# Revit family: Legrand_ElectricFireStopping_EZPathFirestopModule_Series44_Wall
name_source: partatom
category: Equipement spécialisé
units: mm (PartAtom-declared; Revit-internal decimal feet)

## family parameters
Cote de connecteur circulaire = Utiliser le diamètre
Couper avec des vides une fois chargée = Non
Hôte = Mur
Numéro OmniClass = 23.20.50.14
Partagée = Non
Point de calcul de pièce = Non
Titre OmniClass = Firestopping
Toujours verticalement = Oui
Type d'élément = Normal

## types (13) — shared parameters
AirLeakage(UL1479) = 1.57 m3/h 0% cable, 3.24 m3/h 100% cable
AssetType = Fixed
Classification(EN13501-2) = EI 120
ClassificationName = Uniclass2015
ClassificationValue = Ss_25_60_30
Code d'assemblage = D4030900
CodePerformance = Conforms to the European standard EN1366-3, BS476/20, ASTM E814 and DIN4102-9
Color = Red
Description = EZ-Path is a mechanical device that provides fully compliant fire stopping for power and data cable management pathways.
DocumentationInstallationGuide = https://www.legrand.co.uk
DocumentationLiterature = https://specifi.bimstore.co.uk
DocumentationTechnical = https://www.legrand.co.uk
DurationUnit = Years
EZ-Path 1 = Oui
EZPathDevice = Firestop-STI-EZ_Path-Series_44+_Fire_Rated_Pathway
EZPathDeviceHeight = 117 mm
EZPathDeviceWidth = 102 mm
EZPathLoadingHeight = 86 mm
EZPathLoadingWidth = 95 mm
ExpansionBegins = 177 deg C
Fabricant = Legrand Electric Ltd
Features = The modules, which are suitable for all types of wall, can be assembled and installed horizontally or vertically to form a sturdy unit
Finish = Powder Coated
FireRating = Up to 4 Hr
FireResistance(EN1366-3) = 2 Hours
General Conditions of Use = https://export.legrand.com
IfcExportAs = IfcBuildingElementPart
IfcExportType = IfcBuildingElementPartTypeEnum.FIRESTOP
InServiceTemperature = Not to exceed 49 deg C
ManufacturerName = Legrand Electric Ltd
Material = 1.5mm thk Galv Steel
ModelNumber = CM250058
ModelNumberDevice = CM250058
ModelNumberExtensions = CM250178
ModelReference = EZ-Path® Permanent Automatic Mechanical Firestop System (Series 44) Wall
Modèle = EZ-Path® Permanent Automatic Mechanical Firestop System (Series 44) Wall
NBSDescription = Fire stopping systems
NBSObjectName = Legrand Electric Ltd - Fire stopping systems
NBSReference = 30-85-30
NominalHeight = 120 mm
Note d'identification = P12
PlateCutoutCenterWidth = 52 mm
PlateCutoutHeight = 117 mm
PlateEdgeCenterWidth = 89 mm
ProductPage = https://www.legrand.co.uk
ProductionYear = 2017
ReactionToFire(EN13501-1) = Class E
ReferencedStandard = CE Marking, EN 1366-3, ETA 130993
Region = Europe
RetainingPlate = Firestop-STI-EZ_Path-Retaining_Plate
SafetyDataSheet = https://files.stifirestop.com
SecondaryModelNumberDevice = EZD44T
SecondaryModelNumberExtensions = EZD44ES
Shape = Rectangle (Series 44)
ShelfLife = No Limit
SoundInsulation(ASTME90) = STC 54
TPlate = Non
TestedSystems = https://www.legrand.co.uk
URL = https://www.legrand.co.uk
VolumeExpansion = 800%
WallOpeningCenterWidth = 54 mm
WallOpeningHeight = 120 mm
WarrantyDescription = Firestop certification guaranteed throughout the entire lifetime of the electrical installation
WarrantyDurationLabor = 0
WarrantyDurationParts = 0
WarrantyDurationUnit = Years
Weight(Kg) = 2.67 kg
_BSBibleVersion = 15
_CurrentRevision = 2
_DistributedBy = www.bimstore.co.uk
zero-valued in all types: Elévation par défaut, ExpectedLife, TPlateNo, _BimSpecGuid

## per-type parameters (varying)
| type | BIMObjectName | Commentaires du type | EZ-Path 2 | EZ-Path 3 | EZ-Path 4 | EZ-Path 5 | EZPathCenterOfGang | ModelNumberBrackets | NoOfDevices | NominalWidth | Plate | PlateCutoutWidth | PlateHeight | PlateNo | PlateWidth | SecondaryModelNumberBrackets | Size | TypeName | WallOpeningWidth |
| 1 Device Cast In Place (Concrete Walls Only) Ref 250058 | Legrand_ElectricFireStopping_EZPathFirestopModule_Series44_Wall_1DeviceCastInPlace | 1 Device Cast In Place (Concrete Walls Only) | Non | Non | Non | Non | 51 mm |  | 1 | 108 mm | Non | 105 mm | 270 mm | 0 | 178 mm |  | 120x108mm | 1 Device Cast In Place (Concrete Walls Only) | 108 mm |
| 5 Devices with European Gang Wall Plate Ref 5 x 250058 + 350702 | Legrand_ElectricFireStopping_EZPathFirestopModule_Series44_Wall_5DeviceGangWallPlate_European | 5 Devices with European Gang Wall Plate | Oui | Oui | Oui | Oui | 254 mm | CM350702 | 5 | 514 mm | Oui | 511 mm | 191 mm  [stored 0.62664 ft] | 1 | 584 mm | EZP544WE | 120x514mm | 5 Devices with European Gang Wall Plate | 514 mm |
| 4 Devices with European Gang Wall Plate Ref 4 x 250058 + 350702 | Legrand_ElectricFireStopping_EZPathFirestopModule_Series44_Wall_4DeviceGangWallPlate_European | 4 Devices with European Gang Wall Plate | Oui | Oui | Oui | Non | 203 mm | CM350702 | 4 | 413 mm | Oui | 410 mm | 191 mm  [stored 0.62664 ft] | 1 | 483 mm | EZP544WE | 120x413mm | 4 Devices with European Gang Wall Plate | 413 mm |
| 3 Devices with European Gang Wall Plate Ref 3 x 250058 + 350702 | Legrand_ElectricFireStopping_EZPathFirestopModule_Series44_Wall_3DeviceGangWallPlate_European | 3 Devices with European Gang Wall Plate | Oui | Oui | Non | Non | 152 mm | CM350702 | 3 | 311 mm | Oui | 308 mm | 191 mm  [stored 0.62664 ft] | 1 | 381 mm | EZP544WE | 120x311mm | 3 Devices with European Gang Wall Plate | 311 mm |
| 2 Devices with European Gang Wall Plate Ref 2 x 250058 + 350702 | Legrand_ElectricFireStopping_EZPathFirestopModule_Series44_Wall_2DeviceGangWallPlate_European | 2 Devices with European Gang Wall Plate | Oui | Non | Non | Non | 102 mm | CM350702 | 2 | 210 mm | Oui | 206 mm | 191 mm  [stored 0.62664 ft] | 1 | 279 mm | EZP544WE | 120x210mm | 2 Devices with European Gang Wall Plate | 210 mm |
| 1 Device with European Gang Wall Plate Ref 250058 + 350702 | Legrand_ElectricFireStopping_EZPathFirestopModule_Series44_Wall_1DeviceGangWallPlate_European | 1 Device with European Gang Wall Plate | Non | Non | Non | Non | 51 mm | CM350702 | 1 | 108 mm | Oui | 105 mm | 191 mm  [stored 0.62664 ft] | 1 | 178 mm | EZP544WE | 120x108mm | 1 Device with European Gang Wall Plate | 108 mm |
| 1 Device with European Wall Plate Ref 250058 + 350700 | Legrand_ElectricFireStopping_EZPathFirestopModule_Series44_Wall_1DeviceWallPlate_European | 1 Device with European Wall Plate | Non | Non | Non | Non | 51 mm | CM350700 | 1 | 108 mm | Oui | 105 mm | 191 mm  [stored 0.62664 ft] | 1 | 178 mm | EZP144WE | 120x108mm | 1 Device with European Wall Plate | 108 mm |
| 2 Device Cast In Place (Concrete Walls Only - Grouted) Ref 2 x 250058 | Legrand_ElectricFireStopping_EZPathFirestopModule_Series44_Wall_2DeviceCastInPlace | 2 Device Cast In Place (Concrete Walls Only - Grouted) | Oui | Non | Non | Non | 102 mm |  | 2 | 210 mm | Non | 206 mm | 270 mm | 0 | 279 mm |  | 120x210mm | 2 Device Cast In Place (Concrete Walls Only - Grouted) | 210 mm |
| 3 Device Cast In Place (Concrete Walls Only - Grouted) Ref 3 x 250058 | Legrand_ElectricFireStopping_EZPathFirestopModule_Series44_Wall_3DeviceCastInPlace | 3 Device Cast In Place (Concrete Walls Only - Grouted) | Oui | Oui | Non | Non | 152 mm |  | 3 | 311 mm | Non | 308 mm | 270 mm | 0 | 381 mm |  | 120x311mm | 3 Device Cast In Place (Concrete Walls Only - Grouted) | 311 mm |
| 4 Device Cast In Place (Concrete Walls Only - Grouted) Ref 4 x 250058 | Legrand_ElectricFireStopping_EZPathFirestopModule_Series44_Wall_4DeviceCastInPlace | 4 Device Cast In Place (Concrete Walls Only - Grouted) | Oui | Oui | Oui | Non | 203 mm |  | 4 | 413 mm | Non | 410 mm | 270 mm | 0 | 483 mm |  | 120x413mm | 4 Device Cast In Place (Concrete Walls Only - Grouted) | 413 mm |
| 5 Device Cast In Place (Concrete Walls Only - Grouted) Ref 5 x 250058 | Legrand_ElectricFireStopping_EZPathFirestopModule_Series44_Wall_5DeviceCastInPlace | 5 Device Cast In Place (Concrete Walls Only - Grouted) | Oui | Oui | Oui | Oui | 254 mm |  | 5 | 514 mm | Non | 511 mm | 270 mm | 0 | 584 mm |  | 120x514mm | 5 Device Cast In Place (Concrete Walls Only - Grouted) | 514 mm |
| 1 Device with European Wall Plate Ref 250058 + 250701 | Legrand_ElectricFireStopping_EZPathFirestopModule_Series44_Wall_1DeviceWallPlate_European | 1 Device with European Wall Plate | Non | Non | Non | Non | 51 mm | CM350701 | 1 | 108 mm | Oui | 105 mm | 191 mm  [stored 0.62664 ft] | 1 | 178 mm | EZP144RSE | 120x108mm | 1 Device with European Wall Plate | 108 mm |
| 1 Device with European Wall Plate Ref 250058 + 250230 | Legrand_ElectricFireStopping_EZPathFirestopModule_Series44_Wall_1DeviceWallPlate_European | 1 Device with European Wall Plate | Non | Non | Non | Non | 51 mm | CM350230 | 1 | 108 mm | Oui | 105 mm | 237 mm  [stored 0.777559 ft] | 1 | 178 mm | EZP144WT | 120x108mm | 1 Device with European Wall Plate | 108 mm |

note: [stored X ft] marks values corroborated as IEEE doubles in the binary element streams (Revit-internal decimal feet)

## geometry (parser evidence)
native form markers: Blend x2, Sweep x3
no freeform markers — native parametric forms only
